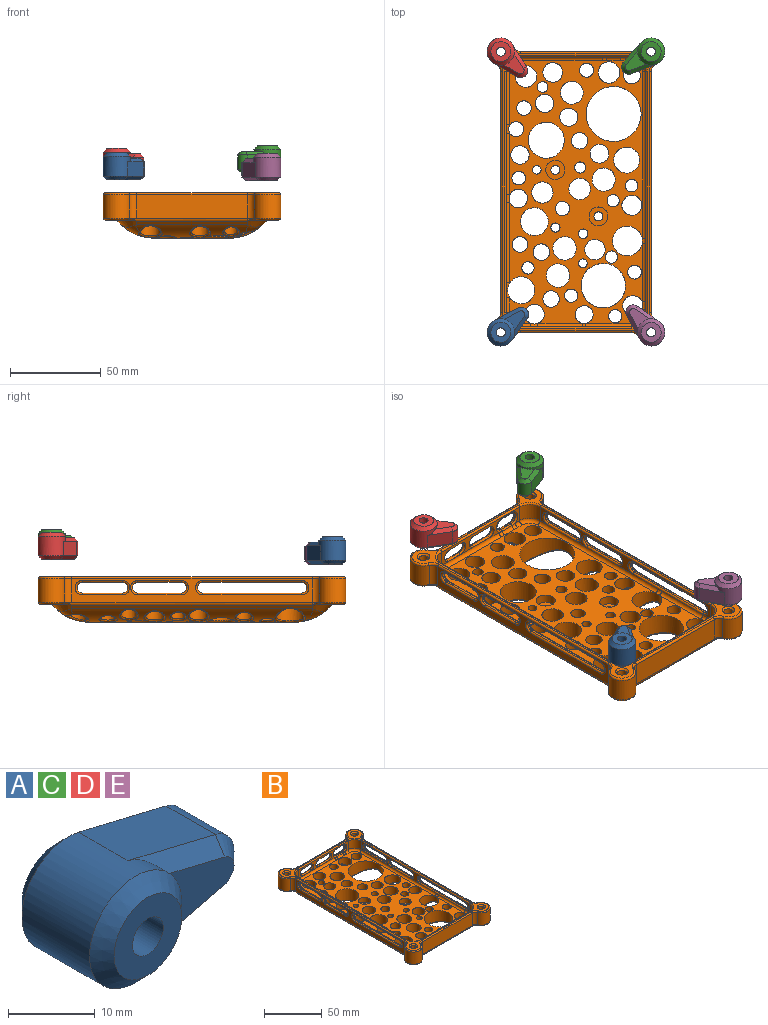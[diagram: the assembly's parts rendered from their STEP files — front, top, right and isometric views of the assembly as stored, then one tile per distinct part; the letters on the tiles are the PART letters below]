
ASSEMBLY  parts=5 mates=4
PART A: 16 faces, bbox 26.5x15x15 mm
  f0: cylinder r=7.5mm len=15mm, axis (0,1,0), area 332.9mm2, adj f4,f5,f7,f9,f12,f14,f15
  f1: cylinder r=2.5mm len=15mm, axis (0,1,0), area 235.6mm2, adj f2,f3
  f2: plane 11x11mm, normal (0,-1,0), area 75.4mm2, adj f1,f15
  f3: plane 22.5x11mm, normal (0,1,0), area 149.7mm2, adj f1,f8,f9,f10,f11
  f4: plane 14.18x8mm, normal (0.23,0,0.97), area 116.7mm2, adj f0,f6,f11,f14
  f5: plane 14.18x8mm, normal (0.23,0,-0.97), area 116.7mm2, adj f0,f6,f8,f12
  f6: cylinder r=4mm len=8mm, axis (0,1,0), area 85.5mm2, adj f4,f5,f10,f13
  f7: plane 10.76x8.32mm, normal (0,-1,0), area 53.6mm2, adj f0,f12,f13,f14
  f8: plane 14.65x5.35mm, normal (0.16,0.71,-0.69), area 41.3mm2, adj f3,f5,f9,f10
  f9: cone r=7.5mm half-angle=45deg, axis (0,-1,0), area 66.4mm2, adj f0,f3,f8,f11
  f10: cone r=4mm half-angle=45deg, axis (0,-1,0), area 22.7mm2, adj f3,f6,f8,f11
  f11: plane 14.65x5.35mm, normal (0.16,0.71,0.69), area 41.3mm2, adj f3,f4,f9,f10
  f12: plane 14.18x5.35mm, normal (0.16,-0.71,-0.69), area 31.4mm2, adj f0,f5,f7,f13
  f13: cone r=2mm half-angle=45deg, axis (0,1,0), area 22.7mm2, adj f6,f7,f12,f14
  f14: plane 14.18x5.35mm, normal (0.16,-0.71,0.69), area 31.4mm2, adj f0,f4,f7,f13
  f15: cone r=5.5mm half-angle=45deg, axis (0,1,0), area 115.5mm2, adj f0,f2
PART B: 380 faces, bbox 99.2x171.2x25 mm
  f0: plane 133x9.04mm, normal (-1,0,0), area 242.7mm2, adj f86,f87,f171,f173,f174,f179,f180,f182
  f1: plane 133x9.15mm, normal (1,0,0), area 243.2mm2, adj f88,f89,f167,f169,f170,f175,f176,f178
  f2: plane 113.74x41.74mm, normal (0,0,-1), area 1665.8mm2, adj f3,f4,f5,f26,f255,f257,f265,f273
  f3: cylinder r=25.67mm len=133mm, axis (0,-1,0), area 936.1mm2, adj f2,f9,f18,f23,f27,f267,f272,f276
  f4: cylinder r=25.67mm len=125.19mm, axis (0,-1,0), area 1073.6mm2, adj f2,f8,f11,f13,f20,f24,f253,f254
  f5: cylinder r=25.67mm len=61mm, axis (1,0,0), area 496.7mm2, adj f2,f9,f14,f20,f23,f258,f260,f263
  f6: cylinder r=2.5mm len=7mm, axis (0,0,1), area 110mm2, adj f150,f317
  f7: cylinder r=2.5mm len=7mm, axis (0,0,1), area 110mm2, adj f148,f316
  f8: bspline ~0.84x0.84mm, area 0.3mm2, adj f4,f21,f256,f262
  f9: bspline ~5.28x5.28mm, area 4.7mm2, adj f3,f5,f268,f309
  f10: bspline ~2.41x2.41mm, area 0.6mm2, adj f25,f26,f270,f283
  f11: plane 0.87x0.72mm, normal (0,0,-1), area 0.3mm2, adj f4,f255,f257
  f12: cone r=11mm half-angle=45deg, axis (0,0,1), area 69.3mm2, adj f13,f14,f20,f78,f244,f366,f369
  f13: plane 133x1.9mm, normal (-0.71,0,-0.71), area 354.3mm2, adj f4,f12,f15,f22,f327,f366
  f14: plane 61x1.9mm, normal (0,0.71,-0.71), area 163.6mm2, adj f5,f12,f16,f368
  f15: cone r=11mm half-angle=45deg, axis (0,0,1), area 69.3mm2, adj f13,f17,f24,f79,f245,f367,f370
  f16: cone r=11mm half-angle=45deg, axis (0,0,1), area 69.3mm2, adj f14,f18,f23,f77,f239,f365,f368
  f17: plane 61x1.9mm, normal (0,-0.71,-0.71), area 163.6mm2, adj f15,f19,f26,f370
  f18: plane 133x1.9mm, normal (0.71,0,-0.71), area 356.7mm2, adj f3,f16,f19,f364
  f19: cone r=11mm half-angle=45deg, axis (0,0,1), area 69.3mm2, adj f17,f18,f27,f80,f250,f364,f371
  f20: bspline ~9.16x9.16mm, area 46.8mm2, adj f4,f5,f12,f261
  f21: cylinder r=25.67mm len=0.77mm, axis (1,0,0), area 0.1mm2, adj f8,f260,f263
  f22: cylinder r=25.67mm len=11.19mm, axis (0,-1,0), area 62.8mm2, adj f13,f24,f326
  f23: bspline ~9.38x9.38mm, area 39.5mm2, adj f3,f5,f16,f306
  f24: bspline ~18.15x18.15mm, area 77.9mm2, adj f4,f15,f22,f26,f252,f328
  f25: cylinder r=25.67mm len=0.41mm, axis (0,-1,0), area 0mm2, adj f10,f276,f281
  f26: cylinder r=25.67mm len=61mm, axis (1,0,0), area 476.1mm2, adj f2,f10,f17,f24,f27,f251,f269,f280
  f27: bspline ~9.75x9.75mm, area 38.4mm2, adj f3,f19,f26,f271
  f28: cylinder r=5.55mm len=11.62mm, axis (0,0,1), area 299.5mm2, adj f81,f269,f270,f271,f276,f346
  f29: cylinder r=12.27mm len=24.55mm, axis (0,0,1), area 891mm2, adj f81,f279,f281,f282,f283
  f30: cylinder r=3.66mm len=10.98mm, axis (0,0,1), area 201mm2, adj f81,f337
  f31: cylinder r=4.94mm len=11.53mm, axis (0,0,1), area 280.2mm2, adj f81,f280,f338
  f32: cylinder r=4.55mm len=12mm, axis (0,0,1), area 332.4mm2, adj f81,f314,f315
  f33: cylinder r=3.66mm len=12mm, axis (0,0,1), area 272.7mm2, adj f81,f312,f313
  f34: cylinder r=5.5mm len=11.65mm, axis (0,0,1), area 299.8mm2, adj f81,f251,f252,f341
  f35: cylinder r=3.82mm len=11.09mm, axis (0,0,1), area 211.9mm2, adj f81,f336
  f36: cylinder r=15.2mm len=30.4mm, axis (0,0,1), area 1008.8mm2, adj f81,f265,f266,f267,f268
  f37: cylinder r=4.72mm len=11.43mm, axis (0,0,1), area 260.1mm2, adj f81,f306,f307,f308,f309
  f38: cylinder r=3.39mm len=12mm, axis (0,0,1), area 254.5mm2, adj f81,f277,f278
  f39: cylinder r=6.43mm len=12.85mm, axis (0,0,1), area 484.3mm2, adj f81,f304,f305
  f40: cylinder r=8.27mm len=16.54mm, axis (0,0,1), area 489.7mm2, adj f81,f272,f273,f350
  f41: cylinder r=3.43mm len=12mm, axis (0,0,1), area 256.5mm2, adj f81,f301,f302
  f42: cylinder r=5.52mm len=11.76mm, axis (0,0,1), area 323.4mm2, adj f81,f300
  f43: cylinder r=3.49mm len=11.42mm, axis (0,0,1), area 212.6mm2, adj f81,f299
  f44: cylinder r=7.18mm len=14.35mm, axis (0,0,1), area 441.4mm2, adj f81,f310,f311
  f45: cylinder r=5.07mm len=12mm, axis (0,0,1), area 382.6mm2, adj f81,f253,f255
  f46: cylinder r=6mm len=12.01mm, axis (0,0,1), area 356.7mm2, adj f81,f259,f261,f262,f263
  f47: cylinder r=9.94mm len=19.89mm, axis (0,0,1), area 749.8mm2, adj f81,f297,f298
  f48: cylinder r=3.76mm len=11.26mm, axis (0,0,1), area 217.7mm2, adj f81,f335
  f49: cylinder r=4.16mm len=10.96mm, axis (0,0,1), area 217.8mm2, adj f81,f334,f357
  f50: cylinder r=2.98mm len=12mm, axis (0,0,1), area 221.4mm2, adj f81,f254,f256,f257,f260
  f51: cylinder r=5.09mm len=11.67mm, axis (0,0,1), area 298.6mm2, adj f81,f296
  f52: cylinder r=4.03mm len=11.84mm, axis (0,0,1), area 263.5mm2, adj f81,f333
  f53: cylinder r=2.37mm len=12mm, axis (0,0,1), area 178.6mm2, adj f81,f294,f295
  f54: cylinder r=4.32mm len=11.54mm, axis (0,0,1), area 257.6mm2, adj f81,f332
  f55: cylinder r=5.88mm len=12mm, axis (0,0,1), area 443.5mm2, adj f81,f292,f293
  f56: cylinder r=7.71mm len=15.42mm, axis (0,0,1), area 581.4mm2, adj f81,f290,f291
  f57: cylinder r=5.13mm len=11.52mm, axis (0,0,1), area 286.3mm2, adj f81,f331,f353
  f58: cylinder r=7.52mm len=15.04mm, axis (0,0,1), area 432.1mm2, adj f81,f326,f327,f328,f329,f349
  f59: cylinder r=3.41mm len=11.97mm, axis (0,0,1), area 238.3mm2, adj f81,f330
  f60: cylinder r=4.57mm len=12mm, axis (0,0,1), area 344.4mm2, adj f81,f287,f288
  f61: cylinder r=6.3mm len=12.6mm, axis (0,0,1), area 475mm2, adj f81,f284,f285
  f62: cylinder r=3.88mm len=11.38mm, axis (0,0,1), area 228.8mm2, adj f81,f325
  f63: cylinder r=5.45mm len=11.85mm, axis (0,0,1), area 331.3mm2, adj f81,f258
  f64: cylinder r=5.94mm len=11.9mm, axis (0,0,1), area 359mm2, adj f81,f264
  f65: cylinder r=3.99mm len=12mm, axis (0,0,1), area 300.6mm2, adj f81,f324
  f66: cylinder r=4.53mm len=12mm, axis (0,0,1), area 341.4mm2, adj f81,f323
  f67: cylinder r=5.91mm len=12mm, axis (0,0,1), area 445.9mm2, adj f81,f303
  f68: cylinder r=3.06mm len=12mm, axis (0,0,1), area 231mm2, adj f81,f322
  f69: cylinder r=5.01mm len=12mm, axis (0,0,1), area 377.6mm2, adj f81,f321
  f70: cylinder r=2.52mm len=12mm, axis (0,0,1), area 190.2mm2, adj f81,f289
  f71: cylinder r=2.45mm len=12mm, axis (0,0,1), area 185mm2, adj f81,f275
  f72: cylinder r=2.66mm len=12mm, axis (0,0,1), area 200.2mm2, adj f81,f320
  f73: cylinder r=5.62mm len=12mm, axis (0,0,1), area 423.4mm2, adj f81,f274
  f74: cylinder r=5.16mm len=12mm, axis (0,0,1), area 389.1mm2, adj f81,f319
  f75: cylinder r=6.48mm len=12.95mm, axis (0,0,1), area 488.4mm2, adj f81,f318
  f76: cylinder r=6.46mm len=12.92mm, axis (0,0,1), area 487mm2, adj f81,f286
  f77: plane 15.52x14.89mm, normal (0,0,-1), area 88.5mm2, adj f16,f239,f240,f241,f368,f374
  f78: plane 15.52x14.89mm, normal (0,0,-1), area 88.5mm2, adj f12,f242,f243,f244,f366,f375
  f79: plane 15.52x14.89mm, normal (0,0,-1), area 88.5mm2, adj f15,f245,f246,f247,f370,f372
  f80: plane 15.52x14.89mm, normal (0,0,-1), area 88.5mm2, adj f19,f248,f249,f250,f364,f373
  f81: plane 145.1x73mm, normal (0,0,1), area 5237.2mm2, adj f28,f29,f30,f31,f32,f33,f34,f35
  f82: plane 3.09x0.01mm, normal (-1,0,0), area 0mm2, adj f223,f350
  f83: plane 61x9mm, normal (0,-1,0), area 186.9mm2, adj f86,f89,f139,f140,f141,f142,f143,f144
  f84: plane 8.38x0.46mm, normal (1,0,0), area 1.9mm2, adj f227,f349
  f85: plane 61x9.03mm, normal (0,1,0), area 549.1mm2, adj f87,f88,f205,f338,f339,f340,f341,f343
  f86: cylinder r=8mm len=9mm, axis (0,0,-1), area 113.1mm2, adj f0,f83,f199,f354
  f87: cylinder r=8mm len=9mm, axis (0,0,-1), area 113.1mm2, adj f0,f85,f203,f342
  f88: cylinder r=8mm len=9mm, axis (0,0,-1), area 113.1mm2, adj f1,f85,f206,f345
  f89: cylinder r=8mm len=9mm, axis (0,0,-1), area 113.1mm2, adj f1,f83,f202,f361
  f90: plane 133.36x13.17mm, normal (-1,0,0), area 797.5mm2, adj f96,f97,f151,f152,f153,f154,f155,f156
  f91: plane 133.36x13.17mm, normal (1,0,0), area 797.5mm2, adj f103,f104,f159,f160,f161,f162,f163,f164
  f92: cylinder r=4.32mm len=13mm, axis (0,0,-1), area 67.2mm2, adj f93,f105,f185,f241
  f93: plane 61.36x13.17mm, normal (0,1,0), area 338.7mm2, adj f92,f94,f187,f211,f212,f213,f214,f215
  f94: cylinder r=4.32mm len=13.17mm, axis (0,0,-1), area 67.2mm2, adj f93,f95,f189,f244,f369
  f95: cylinder r=7.5mm len=14.48mm, axis (0,0,-1), area 386.5mm2, adj f94,f96,f191,f243
  f96: cylinder r=4.32mm len=13mm, axis (0,0,-1), area 67.2mm2, adj f90,f95,f193,f242
  f97: cylinder r=4.32mm len=13.17mm, axis (0,0,-1), area 67.2mm2, adj f90,f98,f197,f245,f367
  f98: cylinder r=7.5mm len=14.48mm, axis (0,0,-1), area 386.5mm2, adj f97,f99,f198,f246
  f99: cylinder r=4.32mm len=13mm, axis (0,0,-1), area 67.2mm2, adj f98,f100,f196,f247
  f100: plane 61.36x13.17mm, normal (0,-1,0), area 803.5mm2, adj f99,f101,f194,f247,f370
  f101: cylinder r=4.32mm len=13.17mm, axis (0,0,-1), area 67.2mm2, adj f100,f102,f192,f250,f371
  f102: cylinder r=7.5mm len=14.48mm, axis (0,0,-1), area 386.5mm2, adj f101,f103,f190,f249
  f103: cylinder r=4.32mm len=13mm, axis (0,0,-1), area 67.2mm2, adj f91,f102,f188,f248
  f104: cylinder r=4.32mm len=13.17mm, axis (0,0,-1), area 67.2mm2, adj f91,f105,f184,f239,f365
  f105: cylinder r=7.5mm len=14.48mm, axis (0,0,-1), area 386.5mm2, adj f92,f104,f183,f240
  f106: plane 168x96mm, normal (0,0,1), area 853.2mm2, adj f183,f184,f185,f186,f187,f188,f189,f190
  f107: cylinder r=2.5mm len=13mm, axis (0,0,-1), area 204.2mm2, adj f374,f378
  f108: cylinder r=2.5mm len=13mm, axis (0,0,-1), area 204.2mm2, adj f372,f377
  f109: cylinder r=2.5mm len=13mm, axis (0,0,-1), area 204.2mm2, adj f373,f379
  f110: cylinder r=2.5mm len=13mm, axis (0,0,-1), area 204.2mm2, adj f375,f376
  f111: cylinder r=3mm len=6mm, axis (-1,0,0), area 9.4mm2, adj f112,f114,f159,f171
  f112: plane 23.94x1mm, normal (0,0,1), area 23.9mm2, adj f111,f113,f160,f172
  f113: cylinder r=3mm len=6mm, axis (-1,0,0), area 9.2mm2, adj f112,f114,f162,f174
  f114: plane 23.99x1mm, normal (0,0,-1), area 24mm2, adj f111,f113,f161,f173
  f115: cylinder r=3mm len=6mm, axis (-1,0,0), area 9.4mm2, adj f116,f118,f224,f232
  f116: plane 54.5x1mm, normal (0,0,1), area 54.5mm2, adj f115,f117,f223,f231
  f117: cylinder r=3mm len=6mm, axis (-1,0,0), area 9.4mm2, adj f116,f118,f225,f233
  f118: plane 54.5x1mm, normal (0,0,-1), area 54.5mm2, adj f115,f117,f226,f234
  f119: cylinder r=3mm len=6mm, axis (-1,0,0), area 9.4mm2, adj f120,f122,f163,f179
  f120: plane 22.17x1mm, normal (0,0,-1), area 22.2mm2, adj f119,f121,f164,f180
  f121: cylinder r=3mm len=6mm, axis (-1,0,0), area 9.3mm2, adj f120,f122,f166,f182
  f122: plane 22.13x1mm, normal (0,0,1), area 22.1mm2, adj f119,f121,f165,f181
  f123: plane 23.99x1mm, normal (0,0,-1), area 24mm2, adj f124,f126,f156,f169
  f124: cylinder r=3mm len=6mm, axis (-1,0,0), area 9.2mm2, adj f123,f125,f158,f170
  f125: plane 23.94x1mm, normal (0,0,1), area 23.9mm2, adj f124,f126,f157,f168
  f126: cylinder r=3mm len=6mm, axis (-1,0,0), area 9.4mm2, adj f123,f125,f155,f167
  f127: plane 54.5x1mm, normal (0,0,-1), area 54.5mm2, adj f128,f130,f230,f238
  f128: cylinder r=3mm len=6mm, axis (-1,0,0), area 9.4mm2, adj f127,f129,f229,f236
  f129: plane 54.5x1mm, normal (0,0,1), area 54.5mm2, adj f128,f130,f227,f235
  f130: cylinder r=3mm len=6mm, axis (-1,0,0), area 9.4mm2, adj f127,f129,f228,f237
  f131: plane 22.13x1mm, normal (0,0,1), area 22.1mm2, adj f132,f134,f152,f177
  f132: cylinder r=3mm len=6mm, axis (-1,0,0), area 9.3mm2, adj f131,f133,f154,f178
  f133: plane 22.17x1mm, normal (0,0,-1), area 22.2mm2, adj f132,f134,f153,f176
  f134: cylinder r=3mm len=6mm, axis (-1,0,0), area 9.4mm2, adj f131,f133,f151,f175
  f135: plane 7.52x1mm, normal (0,0,1), area 7.5mm2, adj f136,f138,f208,f211
  f136: cylinder r=3.6mm len=7.2mm, axis (0,1,0), area 11.3mm2, adj f135,f137,f210,f212
  f137: plane 7.52x1mm, normal (0,0,-1), area 7.5mm2, adj f136,f138,f209,f214
  f138: cylinder r=3.6mm len=7.2mm, axis (0,1,0), area 11.3mm2, adj f135,f137,f207,f213
  f139: plane 12.06x2mm, normal (0,0,1), area 24.1mm2, adj f83,f140,f142,f215
  f140: cylinder r=3.6mm len=7.2mm, axis (0,1,0), area 22.6mm2, adj f83,f139,f141,f216
  f141: plane 12.06x2mm, normal (0,0,-1), area 24.1mm2, adj f83,f140,f142,f218
  f142: cylinder r=3.6mm len=7.2mm, axis (0,1,0), area 22.6mm2, adj f83,f139,f141,f217
  f143: cylinder r=3.6mm len=7.2mm, axis (0,1,0), area 22.6mm2, adj f83,f144,f146,f220
  f144: plane 9.26x2mm, normal (0,0,-1), area 18.5mm2, adj f83,f143,f145,f222
  f145: cylinder r=3.6mm len=7.2mm, axis (0,1,0), area 22.6mm2, adj f83,f144,f146,f221
  f146: plane 9.26x2mm, normal (0,0,1), area 18.5mm2, adj f83,f143,f145,f219
  f147: cylinder r=5.18mm len=10.37mm, axis (0,0,1), area 162.9mm2, adj f81,f148
  f148: plane 10.37x10.37mm, normal (0,0,1), area 64.8mm2, adj f7,f147
  f149: cylinder r=5.27mm len=10.54mm, axis (0,0,1), area 165.6mm2, adj f81,f150
  f150: plane 10.54x10.54mm, normal (0,0,1), area 67.6mm2, adj f6,f149
  f151: torus R=4mm, axis (1,0,0), area 16.6mm2, adj f90,f134,f152,f153
  f152: cylinder r=1mm len=22.14mm, axis (0,-1,0), area 34.8mm2, adj f90,f131,f151,f154
  f153: cylinder r=1mm len=22.18mm, axis (0,1,0), area 34.8mm2, adj f90,f133,f151,f154
  f154: torus R=4mm, axis (1,0,0), area 16.4mm2, adj f90,f132,f152,f153
  f155: torus R=4mm, axis (1,0,0), area 16.6mm2, adj f90,f126,f156,f157
  f156: cylinder r=1mm len=24.02mm, axis (0,1,0), area 37.7mm2, adj f90,f123,f155,f158
  f157: cylinder r=1mm len=23.96mm, axis (0,-1,0), area 37.6mm2, adj f90,f125,f155,f158
  f158: torus R=4mm, axis (1,0,0), area 16.2mm2, adj f90,f124,f156,f157
  f159: torus R=4mm, axis (1,0,0), area 16.6mm2, adj f91,f111,f160,f161
  f160: cylinder r=1mm len=23.96mm, axis (0,-1,0), area 37.6mm2, adj f91,f112,f159,f162
  f161: cylinder r=1mm len=24.02mm, axis (0,1,0), area 37.7mm2, adj f91,f114,f159,f162
  f162: torus R=4mm, axis (1,0,0), area 16.2mm2, adj f91,f113,f160,f161
  f163: torus R=4mm, axis (1,0,0), area 16.6mm2, adj f91,f119,f164,f165
  f164: cylinder r=1mm len=22.18mm, axis (0,1,0), area 34.8mm2, adj f91,f120,f163,f166
  f165: cylinder r=1mm len=22.14mm, axis (0,-1,0), area 34.8mm2, adj f91,f122,f163,f166
  f166: torus R=4mm, axis (1,0,0), area 16.4mm2, adj f91,f121,f164,f165
  f167: torus R=4mm, axis (1,0,0), area 16.6mm2, adj f1,f126,f168,f169
  f168: cylinder r=1mm len=23.96mm, axis (0,-1,0), area 37.6mm2, adj f125,f167,f170,f355
  f169: cylinder r=1mm len=24.02mm, axis (0,1,0), area 37.7mm2, adj f1,f123,f167,f170
  f170: torus R=4mm, axis (1,0,0), area 16.2mm2, adj f1,f124,f168,f169
  f171: torus R=4mm, axis (1,0,0), area 16.6mm2, adj f0,f111,f172,f173
  f172: cylinder r=1mm len=23.96mm, axis (0,1,0), area 37.6mm2, adj f112,f171,f174,f352
  f173: cylinder r=1mm len=24.02mm, axis (0,-1,0), area 37.7mm2, adj f0,f114,f171,f174
  f174: torus R=4mm, axis (1,0,0), area 16.2mm2, adj f0,f113,f172,f173
  f175: torus R=4mm, axis (1,0,0), area 16.6mm2, adj f1,f134,f176,f177
  f176: cylinder r=1mm len=22.18mm, axis (0,1,0), area 34.8mm2, adj f1,f133,f175,f178
  f177: cylinder r=1mm len=22.14mm, axis (0,-1,0), area 34.8mm2, adj f131,f175,f178,f359
  f178: torus R=4mm, axis (1,0,0), area 16.4mm2, adj f1,f132,f176,f177
  f179: torus R=4mm, axis (1,0,0), area 16.6mm2, adj f0,f119,f180,f181
  f180: cylinder r=1mm len=22.18mm, axis (0,-1,0), area 34.8mm2, adj f0,f120,f179,f182
  f181: cylinder r=1mm len=22.14mm, axis (0,1,0), area 34.8mm2, adj f122,f179,f182,f352
  f182: torus R=4mm, axis (1,0,0), area 16.4mm2, adj f0,f121,f180,f181
  f183: torus R=6.5mm, axis (0,0,1), area 44.4mm2, adj f105,f106,f184,f185
  f184: torus R=5.32mm, axis (0,0,1), area 8.8mm2, adj f104,f106,f183,f186
  f185: torus R=5.32mm, axis (0,0,1), area 8.8mm2, adj f92,f106,f183,f187
  f186: cylinder r=1mm len=133mm, axis (0,-1,0), area 208.9mm2, adj f91,f106,f184,f188
  f187: cylinder r=1mm len=61mm, axis (1,0,0), area 95.8mm2, adj f93,f106,f185,f189
  f188: torus R=5.32mm, axis (0,0,1), area 8.8mm2, adj f103,f106,f186,f190
  f189: torus R=5.32mm, axis (0,0,1), area 8.8mm2, adj f94,f106,f187,f191
  f190: torus R=6.5mm, axis (0,0,1), area 44.4mm2, adj f102,f106,f188,f192
  f191: torus R=6.5mm, axis (0,0,1), area 44.4mm2, adj f95,f106,f189,f193
  f192: torus R=5.32mm, axis (0,0,1), area 8.8mm2, adj f101,f106,f190,f194
  f193: torus R=5.32mm, axis (0,0,1), area 8.8mm2, adj f96,f106,f191,f195
  f194: cylinder r=1mm len=61mm, axis (-1,0,0), area 95.8mm2, adj f100,f106,f192,f196
  f195: cylinder r=1mm len=133mm, axis (0,1,0), area 208.9mm2, adj f90,f106,f193,f197
  f196: torus R=5.32mm, axis (0,0,1), area 8.8mm2, adj f99,f106,f194,f198
  f197: torus R=5.32mm, axis (0,0,1), area 8.8mm2, adj f97,f106,f195,f198
  f198: torus R=6.5mm, axis (0,0,1), area 44.4mm2, adj f98,f106,f196,f197
  f199: torus R=9mm, axis (0,0,1), area 20.6mm2, adj f86,f106,f200,f201
  f200: cylinder r=1mm len=61mm, axis (-1,0,0), area 95.8mm2, adj f83,f106,f199,f202
  f201: cylinder r=1mm len=133mm, axis (0,1,0), area 208.9mm2, adj f0,f106,f199,f203
  f202: torus R=9mm, axis (0,0,1), area 20.6mm2, adj f89,f106,f200,f204
  f203: torus R=9mm, axis (0,0,1), area 20.6mm2, adj f87,f106,f201,f205
  f204: cylinder r=1mm len=133mm, axis (0,-1,0), area 208.9mm2, adj f1,f106,f202,f206
  f205: cylinder r=1mm len=61mm, axis (1,0,0), area 95.8mm2, adj f85,f106,f203,f206
  f206: torus R=9mm, axis (0,0,1), area 20.6mm2, adj f88,f106,f204,f205
  f207: torus R=4.6mm, axis (0,1,0), area 19.2mm2, adj f83,f138,f208,f209,f358
  f208: cylinder r=1mm len=7.52mm, axis (-1,0,0), area 9.8mm2, adj f135,f207,f210,f360
  f209: cylinder r=1mm len=7.52mm, axis (1,0,0), area 11.8mm2, adj f83,f137,f207,f210
  f210: torus R=4.6mm, axis (0,1,0), area 19.2mm2, adj f83,f136,f208,f209,f362
  f211: cylinder r=1mm len=7.52mm, axis (1,0,0), area 11.8mm2, adj f93,f135,f212,f213
  f212: torus R=4.6mm, axis (0,1,0), area 19.6mm2, adj f93,f136,f211,f214
  f213: torus R=4.6mm, axis (0,1,0), area 19.6mm2, adj f93,f138,f211,f214
  f214: cylinder r=1mm len=7.52mm, axis (-1,0,0), area 11.8mm2, adj f93,f137,f212,f213
  f215: cylinder r=1mm len=12.06mm, axis (1,0,0), area 18.9mm2, adj f93,f139,f216,f217
  f216: torus R=4.6mm, axis (0,1,0), area 19.6mm2, adj f93,f140,f215,f218
  f217: torus R=4.6mm, axis (0,1,0), area 19.6mm2, adj f93,f142,f215,f218
  f218: cylinder r=1mm len=12.06mm, axis (-1,0,0), area 18.9mm2, adj f93,f141,f216,f217
  f219: cylinder r=1mm len=9.26mm, axis (1,0,0), area 14.5mm2, adj f93,f146,f220,f221
  f220: torus R=4.6mm, axis (0,1,0), area 19.6mm2, adj f93,f143,f219,f222
  f221: torus R=4.6mm, axis (0,1,0), area 19.6mm2, adj f93,f145,f219,f222
  f222: cylinder r=1mm len=9.26mm, axis (-1,0,0), area 14.5mm2, adj f93,f144,f220,f221
  f223: cylinder r=1mm len=54.5mm, axis (0,1,0), area 85.6mm2, adj f82,f116,f224,f225,f348,f352
  f224: torus R=4mm, axis (1,0,0), area 16.6mm2, adj f0,f115,f223,f226
  f225: torus R=4mm, axis (1,0,0), area 16.6mm2, adj f0,f117,f223,f226
  f226: cylinder r=1mm len=54.5mm, axis (0,-1,0), area 85.6mm2, adj f0,f118,f224,f225
  f227: cylinder r=1mm len=54.5mm, axis (0,-1,0), area 85.6mm2, adj f84,f129,f228,f229,f347,f351
  f228: torus R=4mm, axis (1,0,0), area 16.6mm2, adj f1,f130,f227,f230
  f229: torus R=4mm, axis (1,0,0), area 16.6mm2, adj f1,f128,f227,f230
  f230: cylinder r=1mm len=54.5mm, axis (0,1,0), area 85.6mm2, adj f1,f127,f228,f229
  f231: cylinder r=1mm len=54.5mm, axis (0,-1,0), area 85.6mm2, adj f91,f116,f232,f233
  f232: torus R=4mm, axis (1,0,0), area 16.6mm2, adj f91,f115,f231,f234
  f233: torus R=4mm, axis (1,0,0), area 16.6mm2, adj f91,f117,f231,f234
  f234: cylinder r=1mm len=54.5mm, axis (0,1,0), area 85.6mm2, adj f91,f118,f232,f233
  f235: cylinder r=1mm len=54.5mm, axis (0,-1,0), area 85.6mm2, adj f90,f129,f236,f237
  f236: torus R=4mm, axis (1,0,0), area 16.6mm2, adj f90,f128,f235,f238
  f237: torus R=4mm, axis (1,0,0), area 16.6mm2, adj f90,f130,f235,f238
  f238: cylinder r=1mm len=54.5mm, axis (0,1,0), area 85.6mm2, adj f90,f127,f236,f237
  f239: torus R=5.32mm, axis (0,0,1), area 6.2mm2, adj f16,f77,f104,f240,f365
  f240: torus R=6.5mm, axis (0,0,1), area 44.4mm2, adj f77,f105,f239,f241
  f241: torus R=5.32mm, axis (0,0,1), area 6.6mm2, adj f77,f92,f93,f240,f368
  f242: torus R=5.32mm, axis (0,0,1), area 6.6mm2, adj f78,f90,f96,f243,f366
  f243: torus R=6.5mm, axis (0,0,1), area 44.4mm2, adj f78,f95,f242,f244
  f244: torus R=5.32mm, axis (0,0,1), area 6.2mm2, adj f12,f78,f94,f243,f369
  f245: torus R=5.32mm, axis (0,0,1), area 6.2mm2, adj f15,f79,f97,f246,f367
  f246: torus R=6.5mm, axis (0,0,1), area 44.4mm2, adj f79,f98,f245,f247
  f247: torus R=5.32mm, axis (0,0,1), area 6.6mm2, adj f79,f99,f100,f246,f370
  f248: torus R=5.32mm, axis (0,0,1), area 6.6mm2, adj f80,f91,f103,f249,f364
  f249: torus R=6.5mm, axis (0,0,1), area 44.4mm2, adj f80,f102,f248,f250
  f250: torus R=5.32mm, axis (0,0,1), area 6.2mm2, adj f19,f80,f101,f249,f371
  f251: bspline ~13.53x12.87mm, area 53.6mm2, adj f26,f34,f252
  f252: bspline ~8.35x5.6mm, area 16.9mm2, adj f24,f34,f251
  f253: bspline ~10.76x4.26mm, area 17mm2, adj f4,f45,f255
  f254: bspline ~4.42x2.41mm, area 5.3mm2, adj f4,f50,f256,f257
  f255: torus R=6.07mm, axis (0,0,1), area 36mm2, adj f2,f11,f45,f253,f257
  f256: bspline ~1.15x1.09mm, area 0.8mm2, adj f8,f50,f254,f260
  f257: torus R=3.98mm, axis (0,0,1), area 8.7mm2, adj f2,f11,f50,f254,f255,f260
  f258: bspline ~13.44x12.9mm, area 65.8mm2, adj f5,f63,f260
  f259: bspline ~13.03x9.39mm, area 31.4mm2, adj f4,f46,f261,f262
  f260: bspline ~7.96x5.52mm, area 18.4mm2, adj f5,f21,f50,f256,f257,f258,f263
  f261: bspline ~6.68x6.59mm, area 13.6mm2, adj f20,f46,f259,f263
  f262: bspline ~1.8x1.75mm, area 0.8mm2, adj f8,f46,f259,f263
  f263: bspline ~12.97x9.83mm, area 32.2mm2, adj f5,f21,f46,f260,f261,f262
  f264: bspline ~14.46x13.91mm, area 72.7mm2, adj f5,f64,f266
  f265: torus R=16.2mm, axis (0,0,1), area 63.4mm2, adj f2,f36,f266,f267
  f266: bspline ~13.69x4.33mm, area 17.4mm2, adj f5,f36,f264,f265,f268
  f267: bspline ~32.42x19.99mm, area 93mm2, adj f3,f36,f265,f268
  f268: bspline ~1.23x1.14mm, area 1.2mm2, adj f9,f36,f266,f267
  f269: bspline ~9.07x5.82mm, area 15.8mm2, adj f26,f28,f270,f271
  f270: bspline ~1.79x1.34mm, area 2mm2, adj f10,f28,f269,f276
  f271: bspline ~8.41x4.79mm, area 17.3mm2, adj f27,f28,f269,f276
  f272: bspline ~18.54x17.44mm, area 83mm2, adj f3,f40,f273,f277
  f273: torus R=9.27mm, axis (0,0,1), area 16.8mm2, adj f2,f40,f272,f277,f278
  f274: torus R=6.62mm, axis (0,0,1), area 57.4mm2, adj f2,f73,f278
  f275: torus R=3.45mm, axis (0,0,1), area 27.8mm2, adj f2,f71,f279
  f276: bspline ~13.44x10.89mm, area 39.7mm2, adj f3,f25,f28,f270,f271,f281
  f277: bspline ~8.76x4.29mm, area 13.6mm2, adj f3,f38,f272,f273,f278,f281
  f278: torus R=4.39mm, axis (0,0,1), area 17.9mm2, adj f2,f38,f273,f274,f277,f279,f281
  f279: torus R=13.27mm, axis (0,0,1), area 45.8mm2, adj f2,f29,f275,f278,f281,f282
  f280: bspline ~12.38x11.9mm, area 61.8mm2, adj f26,f31,f282
  f281: bspline ~22.6x10.64mm, area 41.2mm2, adj f3,f25,f29,f276,f277,f278,f279,f283
  f282: bspline ~23.3x11.27mm, area 44.3mm2, adj f26,f29,f279,f280,f283
  f283: bspline ~1.98x1.96mm, area 1.9mm2, adj f10,f29,f281,f282
  f284: torus R=7.3mm, axis (0,0,1), area 38.8mm2, adj f2,f61,f285
  f285: bspline ~14.42x7.18mm, area 29.3mm2, adj f5,f61,f284
  f286: torus R=7.46mm, axis (0,0,1), area 67.3mm2, adj f2,f76,f287
  f287: torus R=5.57mm, axis (0,0,1), area 29.3mm2, adj f2,f60,f286,f288
  f288: bspline ~10.94x5.33mm, area 20.6mm2, adj f4,f60,f287
  f289: torus R=3.52mm, axis (0,0,1), area 28.4mm2, adj f2,f70,f290
  f290: torus R=8.71mm, axis (0,0,1), area 33.6mm2, adj f2,f56,f289,f291
  f291: bspline ~17.44x13.13mm, area 53.4mm2, adj f4,f56,f290
  f292: bspline ~13.44x6.39mm, area 25.9mm2, adj f4,f55,f293
  f293: torus R=6.88mm, axis (0,0,1), area 37.6mm2, adj f2,f55,f292
  f294: bspline ~6.75x5.06mm, area 16.5mm2, adj f4,f53,f295
  f295: torus R=3.37mm, axis (0,0,1), area 11.5mm2, adj f2,f53,f294
  f296: bspline ~12.69x12.2mm, area 62.9mm2, adj f4,f51,f297
  f297: bspline ~21.44x9.23mm, area 41.3mm2, adj f4,f47,f296,f298
  f298: torus R=10.94mm, axis (0,0,1), area 64.4mm2, adj f2,f47,f297
  f299: bspline ~9.36x8.99mm, area 43.2mm2, adj f3,f43,f300
  f300: bspline ~13.58x13.05mm, area 68.2mm2, adj f3,f42,f299,f302
  f301: torus R=4.43mm, axis (0,0,1), area 19.6mm2, adj f2,f41,f302
  f302: bspline ~8.86x5.29mm, area 19mm2, adj f3,f41,f300,f301
  f303: torus R=6.91mm, axis (0,0,1), area 61.9mm2, adj f2,f67,f304
  f304: torus R=7.43mm, axis (0,0,1), area 51.7mm2, adj f2,f39,f303,f305
  f305: bspline ~11.96x3.71mm, area 15.7mm2, adj f3,f39,f304
  f306: bspline ~8.32x5.33mm, area 16.5mm2, adj f23,f37,f307,f308
  f307: bspline ~11.51x7.74mm, area 28.3mm2, adj f3,f37,f306,f309
  f308: bspline ~8.38x5.77mm, area 16.9mm2, adj f5,f37,f306,f309
  f309: bspline ~1.71x1.5mm, area 2.2mm2, adj f9,f37,f307,f308
  f310: bspline ~16.34x15.88mm, area 74mm2, adj f3,f44,f311
  f311: torus R=8.18mm, axis (0,0,1), area 12.3mm2, adj f2,f44,f310
  f312: torus R=4.66mm, axis (0,0,1), area 18.9mm2, adj f2,f33,f313
  f313: bspline ~9.32x6.27mm, area 22.4mm2, adj f26,f33,f312
  f314: bspline ~11.12x9.19mm, area 33.8mm2, adj f26,f32,f315
  f315: torus R=5.55mm, axis (0,0,1), area 18mm2, adj f2,f32,f314
  f316: torus R=3.5mm, axis (0,0,1), area 28.3mm2, adj f2,f7
  f317: torus R=3.5mm, axis (0,0,1), area 28.3mm2, adj f2,f6
  f318: torus R=7.48mm, axis (0,0,1), area 67.5mm2, adj f2,f75
  f319: torus R=6.16mm, axis (0,0,1), area 54.5mm2, adj f2,f74
  f320: torus R=3.66mm, axis (0,0,1), area 29.8mm2, adj f2,f72
  f321: torus R=6.01mm, axis (0,0,1), area 53mm2, adj f2,f69
  f322: torus R=4.06mm, axis (0,0,1), area 33.8mm2, adj f2,f68
  f323: torus R=5.53mm, axis (0,0,1), area 48.3mm2, adj f2,f66
  f324: torus R=4.99mm, axis (0,0,1), area 42.9mm2, adj f2,f65
  f325: bspline ~10.17x9.78mm, area 48.3mm2, adj f5,f62
  f326: bspline ~11.83x7.57mm, area 25.9mm2, adj f22,f58,f327,f328
  f327: bspline ~5.54x2.12mm, area 11.9mm2, adj f13,f58,f326,f329
  f328: bspline ~6.7x4.52mm, area 8.6mm2, adj f24,f58,f326,f329
  f329: bspline ~17.25x13.05mm, area 47.6mm2, adj f4,f58,f327,f328,f330
  f330: bspline ~9.18x8.83mm, area 40.5mm2, adj f4,f59,f329
  f331: bspline ~12.77x12.28mm, area 64.4mm2, adj f4,f57
  f332: bspline ~11.09x10.67mm, area 53.4mm2, adj f4,f54
  f333: bspline ~10.47x10.07mm, area 48.5mm2, adj f4,f52
  f334: bspline ~10.76x10.34mm, area 53.5mm2, adj f4,f49
  f335: bspline ~9.91x9.53mm, area 47.1mm2, adj f4,f48
  f336: bspline ~10.05x9.66mm, area 48.5mm2, adj f3,f35
  f337: bspline ~9.71x9.33mm, area 46.7mm2, adj f26,f30
  f338: bspline ~2.35x2.08mm, area 5.1mm2, adj f31,f85,f339,f340
  f339: cylinder r=2mm len=24.72mm, axis (-1,0,0), area 77.7mm2, adj f81,f85,f338,f341
  f340: cylinder r=2mm len=25.17mm, axis (-1,0,0), area 79.1mm2, adj f81,f85,f338,f342
  f341: bspline ~4.86x2.29mm, area 11.3mm2, adj f34,f85,f339,f343
  f342: torus R=6mm, axis (0,0,1), area 35.9mm2, adj f81,f87,f340,f344
  f343: cylinder r=2mm len=5.55mm, axis (-1,0,0), area 17.4mm2, adj f81,f85,f341,f345
  f344: cylinder r=2mm len=2mm, axis (0,-1,0), area 5.3mm2, adj f0,f81,f342,f346
  f345: torus R=6mm, axis (0,0,1), area 35.9mm2, adj f81,f88,f343,f347
  f346: bspline ~5.66x2.33mm, area 11.9mm2, adj f0,f28,f344,f348
  f347: cylinder r=2mm len=8.16mm, axis (0,1,0), area 25.6mm2, adj f1,f81,f227,f345,f349
  f348: cylinder r=2mm len=32.07mm, axis (0,-1,0), area 100.8mm2, adj f0,f81,f223,f346,f350
  f349: bspline ~8.38x2mm, area 18.8mm2, adj f58,f84,f347,f351
  f350: bspline ~3.9x2.1mm, area 9.4mm2, adj f40,f82,f348,f352
  f351: cylinder r=2mm len=44.22mm, axis (0,1,0), area 138.9mm2, adj f1,f81,f227,f349,f353
  f352: cylinder r=2mm len=91.98mm, axis (0,-1,0), area 289mm2, adj f0,f81,f172,f181,f223,f350,f354
  f353: bspline ~5.91x2.58mm, area 12.1mm2, adj f1,f57,f351,f355
  f354: torus R=6mm, axis (0,0,1), area 35.9mm2, adj f81,f86,f352,f356
  f355: cylinder r=2mm len=33.78mm, axis (0,1,0), area 106.1mm2, adj f1,f81,f168,f353,f357
  f356: cylinder r=2mm len=3.44mm, axis (1,0,0), area 10.8mm2, adj f81,f83,f354,f358
  f357: bspline ~4.82x2mm, area 12.6mm2, adj f1,f49,f355,f359
  f358: bspline ~3.33x2.03mm, area 7.2mm2, adj f81,f207,f356,f360
  f359: cylinder r=2mm len=29.34mm, axis (0,1,0), area 92.2mm2, adj f1,f81,f177,f357,f361
  f360: cylinder r=2mm len=7.52mm, axis (-1,0,0), area 19.7mm2, adj f81,f208,f358,f362
  f361: torus R=6mm, axis (0,0,1), area 35.9mm2, adj f81,f89,f359,f363
  f362: bspline ~3.59x2.15mm, area 7.2mm2, adj f81,f210,f360,f363
  f363: cylinder r=2mm len=44.92mm, axis (1,0,0), area 141.1mm2, adj f81,f83,f361,f362
  f364: cylinder r=2mm len=135.84mm, axis (0,1,0), area 211mm2, adj f18,f19,f80,f91,f248,f365
  f365: bspline ~3.35x2.32mm, area 2.6mm2, adj f16,f104,f239,f364
  f366: cylinder r=2mm len=135.84mm, axis (0,1,0), area 211mm2, adj f12,f13,f78,f90,f242,f367
  f367: bspline ~3.35x2.32mm, area 2.6mm2, adj f15,f97,f245,f366
  f368: cylinder r=2mm len=63.84mm, axis (-1,0,0), area 97.9mm2, adj f14,f16,f77,f93,f241,f369
  f369: bspline ~3.35x2.32mm, area 2.6mm2, adj f12,f94,f244,f368
  f370: cylinder r=2mm len=63.84mm, axis (-1,0,0), area 97.9mm2, adj f15,f17,f79,f100,f247,f371
  f371: bspline ~3.35x2.32mm, area 2.6mm2, adj f19,f101,f250,f370
  f372: cone r=2.5mm half-angle=45deg, axis (0,0,-1), area 26.7mm2, adj f79,f108
  f373: cone r=2.5mm half-angle=45deg, axis (0,0,-1), area 26.7mm2, adj f80,f109
  f374: cone r=2.5mm half-angle=45deg, axis (0,0,-1), area 26.7mm2, adj f77,f107
  f375: cone r=2.5mm half-angle=45deg, axis (0,0,-1), area 26.7mm2, adj f78,f110
  f376: cone r=3.5mm half-angle=45deg, axis (0,0,1), area 26.7mm2, adj f106,f110
  f377: cone r=3.5mm half-angle=45deg, axis (0,0,1), area 26.7mm2, adj f106,f108
  f378: cone r=3.5mm half-angle=45deg, axis (0,0,1), area 26.7mm2, adj f106,f107
  f379: cone r=3.5mm half-angle=45deg, axis (0,0,1), area 26.7mm2, adj f106,f109
PART C: same geometry as A
PART D: same geometry as A
PART E: same geometry as A
PLACE A rot(axis=(-0.88,-0.33,0.33),97.1deg) t=(-41.5,-77.5,22.12)mm
PLACE B at identity fixed
PLACE C rot(axis=(-0.21,0.69,-0.69),155.7deg) t=(41.5,77.5,25.92)mm
PLACE D rot(axis=(-0.87,0.35,-0.35),98deg) t=(-41.5,77.5,24.54)mm
PLACE E rot(axis=(-0.3,-0.67,0.67),146.4deg) t=(41.5,-77.5,21.73)mm
MATE cylindrical C.f0 <-> B.f105  axis (0,0,-1) through (41.5,77.5,25.92)mm
MATE cylindrical A.f0 <-> B.f98  axis (0,0,-1) through (-41.5,-77.5,22.12)mm
MATE cylindrical B.f102 <-> E.f0  axis (0,0,1) through (41.5,-77.5,15)mm
MATE cylindrical D.f0 <-> B.f95  axis (0,0,-1) through (-41.5,77.5,24.54)mm
